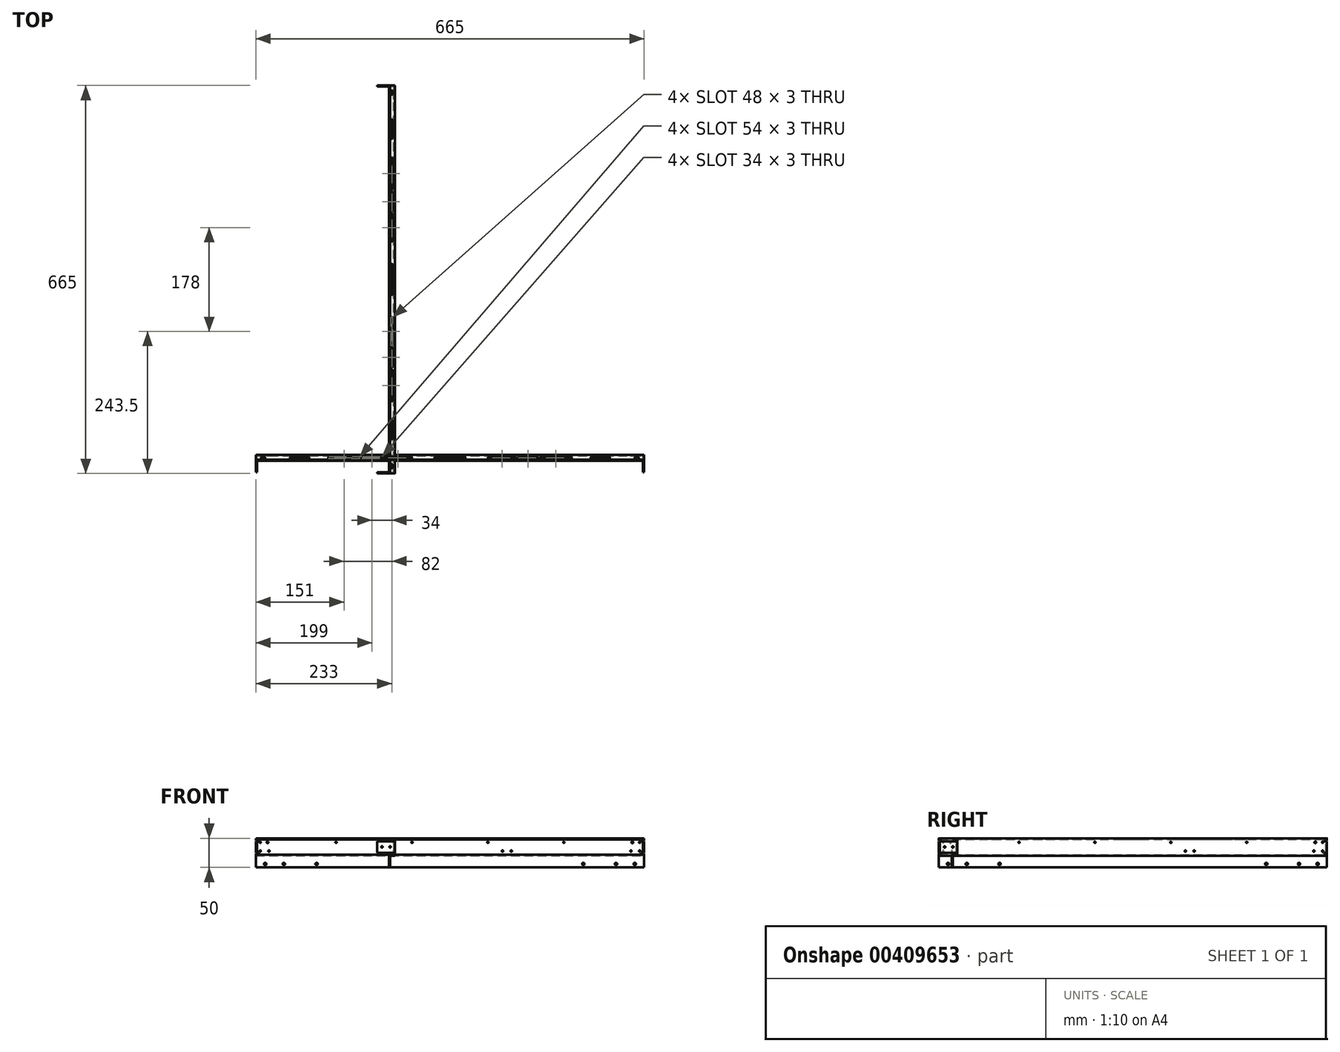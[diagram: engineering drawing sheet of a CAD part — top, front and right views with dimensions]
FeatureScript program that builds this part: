
annotation { "Feature Type Name" : "Feature", "Feature Type Description" : "" }
export const myFeature = defineFeature(function(context is Context, id is Id, definition is map)
    precondition{}
    {
        {
            var Q0;
            Q0=qCreatedBy(makeId("Front.planeOp"),FACE);
            var sketch = newSketch(context, id + "F0", { "sketchPlane" : qUnion([Q0])});
            skLineSegment(sketch, "E0", {"start": v(-20, 60) * mm, "end": v(-12, 60) * mm});
            skLineSegment(sketch, "E1", {"start": v(-12, 60) * mm, "end": v(-12, 58) * mm});
            skLineSegment(sketch, "E2", {"start": v(-12, 58) * mm, "end": v(-18, 58) * mm});
            skLineSegment(sketch, "E3", {"start": v(-18, 58) * mm, "end": v(-18, 32) * mm});
            skLineSegment(sketch, "E4", {"start": v(-20, 30) * mm, "end": v(-20, 60) * mm});
            skLineSegment(sketch, "E5.bottom", {"start": v(-18, 32) * mm, "end": v(-10, 32) * mm});
            skLineSegment(sketch, "E5.top", {"start": v(-20, 30) * mm, "end": v(-12, 30) * mm});
            skLineSegment(sketch, "E6.top", {"start": v(-10, 10) * mm, "end": v(-12, 10) * mm});
            skLineSegment(sketch, "E6.left", {"start": v(-10, 32) * mm, "end": v(-10, 10) * mm});
            skLineSegment(sketch, "E6.right", {"start": v(-12, 30) * mm, "end": v(-12, 10) * mm});
            skSolve(sketch);
        }
        {
            var Q0;
            Q0 = qSketchRegion(id + "F0", true);
            extrude(context, id + "F1", {"entities" : qUnion([Q0]), "depth" : 665 * mm});
        }
        {
            var Q0;
            Q0=makeQuery(id+"F1.opExtrude","SWEPT_FACE",FACE,{"disambiguationData":[OSD([sQuery(id+"F0.wireOp",EDGE,"E3")])]});
            var sketch = newSketch(context, id + "F2", { "sketchPlane" : qUnion([Q0])});
            skLineSegment(sketch, "E7.bottom", {"start": v(0, 35) * mm, "end": v(-2, 35) * mm});
            skLineSegment(sketch, "E7.top", {"start": v(0, 55) * mm, "end": v(-2, 55) * mm});
            skLineSegment(sketch, "E7.left", {"start": v(0, 35) * mm, "end": v(0, 55) * mm});
            skLineSegment(sketch, "E7.right", {"start": v(-2, 35) * mm, "end": v(-2, 55) * mm});
            skLineSegment(sketch, "E8.bottom", {"start": v(-665, 55) * mm, "end": v(-663, 55) * mm});
            skLineSegment(sketch, "E8.top", {"start": v(-665, 35) * mm, "end": v(-663, 35) * mm});
            skLineSegment(sketch, "E8.left", {"start": v(-665, 55) * mm, "end": v(-665, 35) * mm});
            skLineSegment(sketch, "E8.right", {"start": v(-663, 55) * mm, "end": v(-663, 35) * mm});
            skSolve(sketch);
        }
        {
            var Q0;
            Q0 = qSketchRegion(id + "F2", true);
            extrude(context, id + "F3", {"entities" : qUnion([Q0]), "operationType" : NewBodyOperationType.ADD, "depth" : 28 * mm});
        }
        {
            var Q0;
            Q0=makeQuery(id+"F1.opExtrude","SWEPT_FACE",FACE,{"disambiguationData":[OSD([sQuery(id+"F0.wireOp",EDGE,"E0")])]});
            var sketch = newSketch(context, id + "F4", { "sketchPlane" : qUnion([Q0])});
            skLineSegment(sketch, "E9.bottom", {"start": v(130, 0) * mm, "end": v(-20, 0) * mm, "construction": true});
            skLineSegment(sketch, "E9.top", {"start": v(130, -75) * mm, "end": v(-20, -75) * mm, "construction": true});
            skLineSegment(sketch, "E9.left", {"start": v(130, 0) * mm, "end": v(130, -75) * mm, "construction": true});
            skLineSegment(sketch, "E9.right", {"start": v(-20, 0) * mm, "end": v(-20, -75) * mm});
            skLineSegment(sketch, "E10.0", {"start": v(-20, -665) * mm, "end": v(-20, 0) * mm, "construction": true});
            skLineSegment(sketch, "E11.bottom", {"start": v(-20, -75) * mm, "end": v(130, -75) * mm, "construction": true});
            skLineSegment(sketch, "E11.top", {"start": v(-20, -140) * mm, "end": v(130, -140) * mm, "construction": true});
            skLineSegment(sketch, "E11.left", {"start": v(-20, -75) * mm, "end": v(-20, -140) * mm});
            skLineSegment(sketch, "E11.right", {"start": v(130, -75) * mm, "end": v(130, -140) * mm, "construction": true});
            skLineSegment(sketch, "E12.top", {"start": v(-20, -163) * mm, "end": v(130, -163) * mm, "construction": true});
            skLineSegment(sketch, "E12.left", {"start": v(-20, -140) * mm, "end": v(-20, -163) * mm});
            skLineSegment(sketch, "E12.right", {"start": v(130, -140) * mm, "end": v(130, -163) * mm, "construction": true});
            skLineSegment(sketch, "E13.top", {"start": v(-20, -243.5) * mm, "end": v(130, -243.5) * mm, "construction": true});
            skLineSegment(sketch, "E13.left", {"start": v(-20, -163) * mm, "end": v(-20, -243.5) * mm});
            skLineSegment(sketch, "E13.right", {"start": v(130, -163) * mm, "end": v(130, -243.5) * mm, "construction": true});
            skLineSegment(sketch, "E14.top", {"start": v(-20, -332.5) * mm, "end": v(130, -332.5) * mm, "construction": true});
            skLineSegment(sketch, "E14.left", {"start": v(-20, -243.5) * mm, "end": v(-20, -332.5) * mm});
            skLineSegment(sketch, "E14.right", {"start": v(130, -243.5) * mm, "end": v(130, -332.5) * mm, "construction": true});
            skLineSegment(sketch, "E15.top", {"start": v(-20, -462.5) * mm, "end": v(130, -462.5) * mm, "construction": true});
            skLineSegment(sketch, "E15.left", {"start": v(-20, -332.5) * mm, "end": v(-20, -462.5) * mm});
            skLineSegment(sketch, "E15.right", {"start": v(130, -332.5) * mm, "end": v(130, -462.5) * mm, "construction": true});
            skLineSegment(sketch, "E16.top", {"start": v(-20, -485.5) * mm, "end": v(130, -485.5) * mm, "construction": true});
            skLineSegment(sketch, "E16.left", {"start": v(-20, -462.5) * mm, "end": v(-20, -485.5) * mm});
            skLineSegment(sketch, "E16.right", {"start": v(130, -462.5) * mm, "end": v(130, -485.5) * mm, "construction": true});
            skLineSegment(sketch, "E17.top", {"start": v(-20, -665) * mm, "end": v(130, -665) * mm, "construction": true});
            skLineSegment(sketch, "E17.left", {"start": v(-20, -485.5) * mm, "end": v(-20, -665) * mm});
            skLineSegment(sketch, "E17.right", {"start": v(130, -485.5) * mm, "end": v(130, -665) * mm, "construction": true});
            skCircle(sketch, "E18", {"center": v(-15, -12.5) * mm, "radius": 1.5 * mm, "construction": true});
            skCircle(sketch, "E19", {"center": v(-15, -652.5) * mm, "radius": 1.5 * mm, "construction": true});
            skLineSegment(sketch, "E20.bottom", {"start": v(-13.5, -14.5) * mm, "end": v(-16.5, -14.5) * mm, "construction": true});
            skLineSegment(sketch, "E20.top", {"start": v(-13.5, -10.5) * mm, "end": v(-16.5, -10.5) * mm, "construction": true});
            skLineSegment(sketch, "E20.left", {"start": v(-13.5, -14.5) * mm, "end": v(-13.5, -10.5) * mm});
            skLineSegment(sketch, "E20.right", {"start": v(-16.5, -14.5) * mm, "end": v(-16.5, -10.5) * mm});
            skArc(sketch, "E21", {"start": v(-13.5, -10.5) * mm, "mid": v(-15, -9) * mm, "end": v(-16.5, -10.5) * mm});
            skArc(sketch, "E22", {"start": v(-16.5, -14.5) * mm, "mid": v(-15, -16) * mm, "end": v(-13.5, -14.5) * mm});
            skLineSegment(sketch, "E23.bottom", {"start": v(-13.5, -654.5) * mm, "end": v(-16.5, -654.5) * mm, "construction": true});
            skLineSegment(sketch, "E23.top", {"start": v(-13.5, -650.5) * mm, "end": v(-16.5, -650.5) * mm, "construction": true});
            skLineSegment(sketch, "E23.left", {"start": v(-13.5, -654.5) * mm, "end": v(-13.5, -650.5) * mm});
            skLineSegment(sketch, "E23.right", {"start": v(-16.5, -654.5) * mm, "end": v(-16.5, -650.5) * mm});
            skArc(sketch, "E24", {"start": v(-13.5, -650.5) * mm, "mid": v(-15, -649) * mm, "end": v(-16.5, -650.5) * mm});
            skArc(sketch, "E25", {"start": v(-16.5, -654.5) * mm, "mid": v(-15, -656) * mm, "end": v(-13.5, -654.5) * mm});
            skLineSegment(sketch, "E26", {"start": v(29.84, -27) * mm, "end": v(91.74, -27) * mm, "construction": true});
            skLineSegment(sketch, "E27", {"start": v(29.87, -48) * mm, "end": v(95.32, -48) * mm, "construction": true});
            skLineSegment(sketch, "E28.bottom", {"start": v(-13.5, -90) * mm, "end": v(-16.5, -90) * mm, "construction": true});
            skLineSegment(sketch, "E28.top", {"start": v(-13.5, -60) * mm, "end": v(-16.5, -60) * mm, "construction": true});
            skLineSegment(sketch, "E28.left", {"start": v(-13.5, -90) * mm, "end": v(-13.5, -60) * mm});
            skLineSegment(sketch, "E28.right", {"start": v(-16.5, -90) * mm, "end": v(-16.5, -60) * mm});
            skPoint(sketch, "E28.middle", {"position": v(-15, -75) * mm});
            skArc(sketch, "E29", {"start": v(-13.5, -60) * mm, "mid": v(-15, -58.5) * mm, "end": v(-16.5, -60) * mm});
            skArc(sketch, "E30", {"start": v(-16.5, -90) * mm, "mid": v(-15, -91.5) * mm, "end": v(-13.5, -90) * mm});
            skLineSegment(sketch, "E31.bottom", {"start": v(-13.5, -176.5) * mm, "end": v(-16.5, -176.5) * mm, "construction": true});
            skLineSegment(sketch, "E31.top", {"start": v(-13.5, -125.5) * mm, "end": v(-16.5, -125.5) * mm, "construction": true});
            skLineSegment(sketch, "E31.left", {"start": v(-13.5, -176.5) * mm, "end": v(-13.5, -125.5) * mm});
            skLineSegment(sketch, "E31.right", {"start": v(-16.5, -176.5) * mm, "end": v(-16.5, -125.5) * mm});
            skPoint(sketch, "E31.middle", {"position": v(-15, -151) * mm});
            skArc(sketch, "E32", {"start": v(-13.5, -125.5) * mm, "mid": v(-15, -124) * mm, "end": v(-16.5, -125.5) * mm});
            skArc(sketch, "E33", {"start": v(-16.5, -176.5) * mm, "mid": v(-15, -178) * mm, "end": v(-13.5, -176.5) * mm});
            skLineSegment(sketch, "E34", {"start": v(-372.96, -332.5) * mm, "end": v(602.04, -332.5) * mm, "construction": true});
            skLineSegment(sketch, "E35.bottom", {"start": v(-13.5, -266) * mm, "end": v(-16.5, -266) * mm, "construction": true});
            skLineSegment(sketch, "E35.top", {"start": v(-13.5, -221) * mm, "end": v(-16.5, -221) * mm, "construction": true});
            skLineSegment(sketch, "E35.left", {"start": v(-13.5, -266) * mm, "end": v(-13.5, -221) * mm});
            skLineSegment(sketch, "E35.right", {"start": v(-16.5, -266) * mm, "end": v(-16.5, -221) * mm});
            skPoint(sketch, "E35.middle", {"position": v(-15, -243.5) * mm});
            skArc(sketch, "E36", {"start": v(-13.5, -221) * mm, "mid": v(-15, -219.5) * mm, "end": v(-16.5, -221) * mm});
            skArc(sketch, "E37", {"start": v(-16.5, -266) * mm, "mid": v(-15, -267.5) * mm, "end": v(-13.5, -266) * mm});
            skLineSegment(sketch, "E38.bottom", {"start": v(-13.5, -357.5) * mm, "end": v(-16.5, -357.5) * mm, "construction": true});
            skLineSegment(sketch, "E38.top", {"start": v(-13.5, -307.5) * mm, "end": v(-16.5, -307.5) * mm, "construction": true});
            skLineSegment(sketch, "E38.left", {"start": v(-13.5, -357.5) * mm, "end": v(-13.5, -307.5) * mm});
            skLineSegment(sketch, "E38.right", {"start": v(-16.5, -357.5) * mm, "end": v(-16.5, -307.5) * mm});
            skPoint(sketch, "E38.middle", {"position": v(-15, -332.5) * mm});
            skArc(sketch, "E39", {"start": v(-13.5, -307.5) * mm, "mid": v(-15, -306) * mm, "end": v(-16.5, -307.5) * mm});
            skArc(sketch, "E40", {"start": v(-16.5, -357.5) * mm, "mid": v(-15, -359) * mm, "end": v(-13.5, -357.5) * mm});
            skLineSegment(sketch, "E41.bottom", {"start": v(-13.5, -214.5) * mm, "end": v(-16.5, -214.5) * mm, "construction": true});
            skLineSegment(sketch, "E41.top", {"start": v(-13.5, -183.5) * mm, "end": v(-16.5, -183.5) * mm, "construction": true});
            skLineSegment(sketch, "E41.left", {"start": v(-13.5, -214.5) * mm, "end": v(-13.5, -183.5) * mm});
            skLineSegment(sketch, "E41.right", {"start": v(-16.5, -214.5) * mm, "end": v(-16.5, -183.5) * mm});
            skPoint(sketch, "E41.middle", {"position": v(-15, -199) * mm});
            skArc(sketch, "E42", {"start": v(-13.5, -183.5) * mm, "mid": v(-15, -182) * mm, "end": v(-16.5, -183.5) * mm});
            skArc(sketch, "E43", {"start": v(-16.5, -214.5) * mm, "mid": v(-15, -216) * mm, "end": v(-13.5, -214.5) * mm});
            skArc(sketch, "E44.MirrorCS", {"start": v(-16.5, -450.5) * mm, "mid": v(-15, -449) * mm, "end": v(-13.5, -450.5) * mm});
            skLineSegment(sketch, "E45.MirrorCS", {"start": v(-13.5, -481.5) * mm, "end": v(-16.5, -481.5) * mm, "construction": true});
            skArc(sketch, "E46.MirrorCS", {"start": v(-13.5, -539.5) * mm, "mid": v(-15, -541) * mm, "end": v(-16.5, -539.5) * mm});
            skLineSegment(sketch, "E47.MirrorCS", {"start": v(-13.5, -444) * mm, "end": v(-16.5, -444) * mm, "construction": true});
            skArc(sketch, "E48.MirrorCS", {"start": v(-16.5, -399) * mm, "mid": v(-15, -397.5) * mm, "end": v(-13.5, -399) * mm});
            skArc(sketch, "E49.MirrorCS", {"start": v(-16.5, -488.5) * mm, "mid": v(-15, -487) * mm, "end": v(-13.5, -488.5) * mm});
            skArc(sketch, "E50.MirrorCS", {"start": v(-13.5, -444) * mm, "mid": v(-15, -445.5) * mm, "end": v(-16.5, -444) * mm});
            skArc(sketch, "E51.MirrorCS", {"start": v(-13.5, -481.5) * mm, "mid": v(-15, -483) * mm, "end": v(-16.5, -481.5) * mm});
            skLineSegment(sketch, "E52.MirrorCS", {"start": v(-13.5, -539.5) * mm, "end": v(-16.5, -539.5) * mm, "construction": true});
            skLineSegment(sketch, "E53.MirrorCS", {"start": v(-13.5, -488.5) * mm, "end": v(-16.5, -488.5) * mm, "construction": true});
            skLineSegment(sketch, "E54.MirrorCS", {"start": v(-13.5, -399) * mm, "end": v(-16.5, -399) * mm, "construction": true});
            skArc(sketch, "E55.MirrorCS", {"start": v(-16.5, -575) * mm, "mid": v(-15, -573.5) * mm, "end": v(-13.5, -575) * mm});
            skArc(sketch, "E56.MirrorCS", {"start": v(-13.5, -605) * mm, "mid": v(-15, -606.5) * mm, "end": v(-16.5, -605) * mm});
            skLineSegment(sketch, "E57.MirrorCS", {"start": v(-13.5, -605) * mm, "end": v(-16.5, -605) * mm, "construction": true});
            skLineSegment(sketch, "E58.MirrorCS", {"start": v(-13.5, -450.5) * mm, "end": v(-16.5, -450.5) * mm, "construction": true});
            skLineSegment(sketch, "E59.MirrorCS", {"start": v(-13.5, -575) * mm, "end": v(-16.5, -575) * mm, "construction": true});
            skLineSegment(sketch, "E60.MirrorCS", {"start": v(-16.5, -575) * mm, "end": v(-16.5, -605) * mm});
            skLineSegment(sketch, "E61.MirrorCS", {"start": v(-13.5, -575) * mm, "end": v(-13.5, -605) * mm});
            skLineSegment(sketch, "E62.MirrorCS", {"start": v(-13.5, -450.5) * mm, "end": v(-13.5, -481.5) * mm});
            skLineSegment(sketch, "E63.MirrorCS", {"start": v(-16.5, -450.5) * mm, "end": v(-16.5, -481.5) * mm});
            skPoint(sketch, "E64.MirrorP", {"position": v(-15, -466) * mm});
            skPoint(sketch, "E65.MirrorP", {"position": v(-15, -421.5) * mm});
            skPoint(sketch, "E66.MirrorP", {"position": v(-15, -590) * mm});
            skPoint(sketch, "E67.MirrorP", {"position": v(-15, -514) * mm});
            skLineSegment(sketch, "E68.MirrorCS", {"start": v(-16.5, -399) * mm, "end": v(-16.5, -444) * mm});
            skLineSegment(sketch, "E69.MirrorCS", {"start": v(-13.5, -399) * mm, "end": v(-13.5, -444) * mm});
            skLineSegment(sketch, "E70.MirrorCS", {"start": v(-16.5, -488.5) * mm, "end": v(-16.5, -539.5) * mm});
            skLineSegment(sketch, "E71.MirrorCS", {"start": v(-13.5, -488.5) * mm, "end": v(-13.5, -539.5) * mm});
            skPoint(sketch, "E72", {"position": v(-26.56, -12.5) * mm});
            skPoint(sketch, "E73", {"position": v(-24.04, -62.5) * mm});
            skPoint(sketch, "E74", {"position": v(-23.35, -87.5) * mm});
            skPoint(sketch, "E75", {"position": v(-24.4, -127.5) * mm});
            skPoint(sketch, "E76", {"position": v(-25, -145) * mm});
            skPoint(sketch, "E77", {"position": v(-24.92, -158) * mm});
            skPoint(sketch, "E78", {"position": v(-24.79, -174.5) * mm});
            skPoint(sketch, "E79", {"position": v(-24.35, -230) * mm});
            skPoint(sketch, "E80", {"position": v(-25.65, -255) * mm});
            skPoint(sketch, "E81", {"position": v(-24.26, -320) * mm});
            skPoint(sketch, "E82", {"position": v(-23.72, -352.5) * mm});
            skPoint(sketch, "E83", {"position": v(-24.95, -442.5) * mm});
            skPoint(sketch, "E84", {"position": v(-23.34, -467.5) * mm});
            skPoint(sketch, "E85", {"position": v(-22.9, -480.5) * mm});
            skPoint(sketch, "E86", {"position": v(-24.58, -489.5) * mm});
            skPoint(sketch, "E87", {"position": v(-25.98, -652.5) * mm});
            skSolve(sketch);
        }
        {
            var Q0;
            Q0 = qSketchRegion(id + "F4", true);
            extrude(context, id + "F5", {"entities" : qUnion([Q0]), "operationType" : NewBodyOperationType.REMOVE, "oppositeDirection" : true, "depth" : 2 * mm});
        }
        {
            var Q0;
            Q0=makeQuery(id+"F1.opExtrude","SWEPT_FACE",FACE,{"disambiguationData":[OSD([sQuery(id+"F0.wireOp",EDGE,"E6.left")])]});
            var sketch = newSketch(context, id + "F6", { "sketchPlane" : qUnion([Q0])});
            skCircle(sketch, "E88", {"center": v(-16, 16) * mm, "radius": 2.05 * mm});
            skCircle(sketch, "E89", {"center": v(-617, 16) * mm, "radius": 2.05 * mm});
            skCircle(sketch, "E90", {"center": v(-104, 16) * mm, "radius": 2.05 * mm});
            skCircle(sketch, "E91", {"center": v(-7.5, 53) * mm, "radius": 1.2 * mm});
            skCircle(sketch, "E92.1.0.0", {"center": v(-137.5, 53) * mm, "radius": 1.2 * mm});
            skCircle(sketch, "E92.2.0.0", {"center": v(-267.5, 53) * mm, "radius": 1.2 * mm});
            skLineSegment(sketch, "E92.direction1", {"start": v(-7.5, 53) * mm, "end": v(-137.5, 53) * mm, "construction": true});
            skCircle(sketch, "E93.0.3.0", {"center": v(-397.5, 53) * mm, "radius": 1.2 * mm});
            skCircle(sketch, "E93.0.4.0", {"center": v(-527.5, 53) * mm, "radius": 1.2 * mm});
            skCircle(sketch, "E93.0.5.0", {"center": v(-657.5, 53) * mm, "radius": 1.2 * mm});
            skCircle(sketch, "E94", {"center": v(-48, 16) * mm, "radius": 2.05 * mm});
            skCircle(sketch, "E95", {"center": v(-649, 16) * mm, "radius": 2.05 * mm});
            skCircle(sketch, "E96", {"center": v(-561, 16) * mm, "radius": 2.05 * mm});
            skLineSegment(sketch, "E97", {"start": v(-2, 23.79) * mm, "end": v(-2, 13.85) * mm, "construction": true});
            skLineSegment(sketch, "E98", {"start": v(-663, 24.44) * mm, "end": v(-663, 15.87) * mm, "construction": true});
            skLineSegment(sketch, "E99.0", {"start": v(-665, 58) * mm, "end": v(-665, 55) * mm});
            skLineSegment(sketch, "E100.0", {"start": v(-665, 55) * mm, "end": v(-663, 55) * mm});
            skPoint(sketch, "E101.oppositeSnap0", {"position": v(-664, 55) * mm});
            skLineSegment(sketch, "E101.bottom", {"start": v(-665, 56) * mm, "end": v(-660, 56) * mm});
            skLineSegment(sketch, "E101.top", {"start": v(-665, 55) * mm, "end": v(-660, 55) * mm});
            skLineSegment(sketch, "E101.left", {"start": v(-665, 56) * mm, "end": v(-665, 55) * mm});
            skLineSegment(sketch, "E101.right", {"start": v(-660, 56) * mm, "end": v(-660, 55) * mm});
            skLineSegment(sketch, "E102.0", {"start": v(-665, 35) * mm, "end": v(-663, 35) * mm});
            skLineSegment(sketch, "E102.1", {"start": v(-665, 35) * mm, "end": v(-665, 32) * mm});
            skLineSegment(sketch, "E103.bottom", {"start": v(-665, 35) * mm, "end": v(-660, 35) * mm});
            skLineSegment(sketch, "E103.top", {"start": v(-665, 34) * mm, "end": v(-660, 34) * mm});
            skLineSegment(sketch, "E103.left", {"start": v(-665, 35) * mm, "end": v(-665, 34) * mm});
            skLineSegment(sketch, "E103.right", {"start": v(-660, 35) * mm, "end": v(-660, 34) * mm});
            skLineSegment(sketch, "E104.0", {"start": v(0, 58) * mm, "end": v(0, 55) * mm});
            skLineSegment(sketch, "E104.1", {"start": v(0, 55) * mm, "end": v(-2, 55) * mm});
            skLineSegment(sketch, "E104.2", {"start": v(0, 35) * mm, "end": v(-2, 35) * mm});
            skLineSegment(sketch, "E104.3", {"start": v(0, 35) * mm, "end": v(0, 32) * mm});
            skLineSegment(sketch, "E105.bottom", {"start": v(0, 55) * mm, "end": v(-5, 55) * mm});
            skLineSegment(sketch, "E105.top", {"start": v(0, 56) * mm, "end": v(-5, 56) * mm});
            skLineSegment(sketch, "E105.left", {"start": v(0, 55) * mm, "end": v(0, 56) * mm});
            skLineSegment(sketch, "E105.right", {"start": v(-5, 55) * mm, "end": v(-5, 56) * mm});
            skLineSegment(sketch, "E106.bottom", {"start": v(0, 35) * mm, "end": v(-5, 35) * mm});
            skLineSegment(sketch, "E106.top", {"start": v(0, 34) * mm, "end": v(-5, 34) * mm});
            skLineSegment(sketch, "E106.left", {"start": v(0, 35) * mm, "end": v(0, 34) * mm});
            skLineSegment(sketch, "E106.right", {"start": v(-5, 35) * mm, "end": v(-5, 34) * mm});
            skCircle(sketch, "E107", {"center": v(-7.5, 38) * mm, "radius": 1.2 * mm});
            skCircle(sketch, "E108", {"center": v(-657.5, 38) * mm, "radius": 1.2 * mm});
            skCircle(sketch, "E109", {"center": v(-22.5, 38) * mm, "radius": 1.2 * mm});
            skCircle(sketch, "E110", {"center": v(-642.5, 38) * mm, "radius": 1.2 * mm});
            skCircle(sketch, "E111", {"center": v(-227.5, 38) * mm, "radius": 1.2 * mm});
            skCircle(sketch, "E112", {"center": v(-242.5, 38) * mm, "radius": 1.2 * mm});
            skCircle(sketch, "E113", {"center": v(-20, 53) * mm, "radius": 1.5 * mm});
            skCircle(sketch, "E114", {"center": v(-645, 53) * mm, "radius": 1.5 * mm});
            skSolve(sketch);
        }
        {
            var Q0;
            Q0 = qSketchRegion(id + "F6", true);
            extrude(context, id + "F7", {"entities" : qUnion([Q0]), "operationType" : NewBodyOperationType.REMOVE, "oppositeDirection" : true, "depth" : 25 * mm});
        }
        {
            var Q0;
            Q0=makeQuery(id+"F3.boolean.opBoolean","MERGE",FACE,{"derivedFrom":[makeQuery(id+"F1.opExtrude","CAP_FACE",FACE,{"disambiguationData":[OSD([sQuery(id+"F0.wireOp",EDGE,"E0"),sQuery(id+"F0.wireOp",EDGE,"E1"),sQuery(id+"F0.wireOp",EDGE,"E2"),sQuery(id+"F0.wireOp",EDGE,"E3"),sQuery(id+"F0.wireOp",EDGE,"E4"),sQuery(id+"F0.wireOp",EDGE,"E5.bottom"),sQuery(id+"F0.wireOp",EDGE,"E5.top"),sQuery(id+"F0.wireOp",EDGE,"E6.top"),sQuery(id+"F0.wireOp",EDGE,"E6.left"),sQuery(id+"F0.wireOp",EDGE,"E6.right")])],"isStart":false}),makeQuery(id+"F3.opExtrude","SWEPT_FACE",FACE,{"disambiguationData":[OSD([sQuery(id+"F2.wireOp",EDGE,"E8.left")])]})]});
            var sketch = newSketch(context, id + "F8", { "sketchPlane" : qUnion([Q0])});
            skCircle(sketch, "E115", {"center": v(-12, 45) * mm, "radius": 1.2 * mm});
            skPoint(sketch, "E116", {"position": v(10, 45) * mm});
            skCircle(sketch, "E117", {"center": v(2, 45) * mm, "radius": 1.2 * mm});
            skSolve(sketch);
        }
        {
            var Q0;
            Q0 = qSketchRegion(id + "F8", true);
            extrude(context, id + "F9", {"entities" : qUnion([Q0]), "operationType" : NewBodyOperationType.REMOVE, "endBound" : BoundingType.THROUGH_ALL, "oppositeDirection" : true, "depth" : 2 * mm});
        }
        {
            var Q0;
            Q0=makeQuery(id+"F1.opExtrude","SWEPT_EDGE",EDGE,{"disambiguationData":[OSD([sQuery(id+"F0.wireOp",EDGE,"E0"),sQuery(id+"F0.wireOp",EDGE,"E4")])]});
            var Q1;
            Q1=makeQuery(id+"F1.opExtrude","SWEPT_EDGE",EDGE,{"disambiguationData":[OSD([sQuery(id+"F0.wireOp",EDGE,"E2"),sQuery(id+"F0.wireOp",EDGE,"E3")])]});
            var Q2;
            Q2=makeQuery(id+"F1.opExtrude","SWEPT_EDGE",EDGE,{"disambiguationData":[OSD([sQuery(id+"F0.wireOp",EDGE,"E3"),sQuery(id+"F0.wireOp",EDGE,"E5.bottom")])]});
            var Q3;
            Q3=makeQuery(id+"F1.opExtrude","SWEPT_EDGE",EDGE,{"disambiguationData":[OSD([sQuery(id+"F0.wireOp",EDGE,"E5.bottom"),sQuery(id+"F0.wireOp",EDGE,"E6.left")])]});
            var Q4;
            Q4=makeQuery(id+"F1.opExtrude","SWEPT_EDGE",EDGE,{"disambiguationData":[OSD([sQuery(id+"F0.wireOp",EDGE,"E4"),sQuery(id+"F0.wireOp",EDGE,"E5.top")])]});
            var Q5;
            Q5=makeQuery(id+"F1.opExtrude","SWEPT_EDGE",EDGE,{"disambiguationData":[OSD([sQuery(id+"F0.wireOp",EDGE,"E5.top"),sQuery(id+"F0.wireOp",EDGE,"E6.right")])]});
            fillet(context, id + "F10", {"entities" : qUnion([Q0, Q1, Q2, Q3, Q4, Q5]), "radius" : 1 * mm, "tangentPropagation" : true, "allowEdgeOverflow" : false});
        }
        {
            var Q0;
            Q0=makeQuery(id+"F3.opExtrude","CAP_EDGE",EDGE,{"disambiguationData":[OSD([sQuery(id+"F2.wireOp",EDGE,"E8.right")])],"isStart":true});
            var Q1;
            {var subQ0=sQuery(id+"F0.wireOp",EDGE,"E4");Q1=makeQuery(id+"F7.boolean.opBoolean","SPLIT",EDGE,{"disambiguationData":[TD([makeQuery(id+"F3.opExtrude","SWEPT_FACE",FACE,{"disambiguationData":[OSD([sQuery(id+"F2.wireOp",EDGE,"E8.bottom")])]})])],"derivedFrom":makeQuery(id+"F1.opExtrude","CAP_EDGE",EDGE,{"disambiguationData":[OSD([subQ0])],"isStart":false})});}
            var Q2;
            Q2=makeQuery(id+"F3.opExtrude","CAP_EDGE",EDGE,{"disambiguationData":[OSD([sQuery(id+"F2.wireOp",EDGE,"E7.right")])],"isStart":true});
            var Q3;
            {var subQ0=sQuery(id+"F0.wireOp",EDGE,"E4");Q3=makeQuery(id+"F7.boolean.opBoolean","SPLIT",EDGE,{"disambiguationData":[TD([makeQuery(id+"F3.opExtrude","SWEPT_FACE",FACE,{"disambiguationData":[OSD([sQuery(id+"F2.wireOp",EDGE,"E7.bottom")])]})])],"derivedFrom":makeQuery(id+"F1.opExtrude","CAP_EDGE",EDGE,{"disambiguationData":[OSD([subQ0])],"isStart":true})});}
            fillet(context, id + "F11", {"entities" : qUnion([Q0, Q1, Q2, Q3]), "radius" : 1 * mm, "tangentPropagation" : true, "allowEdgeOverflow" : false});
        }
        {
            var Q0;
            Q0=qCreatedBy(makeId("Right.planeOp"),FACE);
            cPlane(context, id + "F12", {"entities" : qUnion([Q0]), "cplaneType" : CPlaneType.OFFSET, "offset" : 113 * mm, "width" : 150 * mm, "height" : 150 * mm});
        }
        {
            var Q0;
            Q0=makeQuery(id+"F1.opExtrude","SWEPT_BODY",BODY,{"disambiguationData":[OSD([sQuery(id+"F0.wireOp",EDGE,"E0"),sQuery(id+"F0.wireOp",EDGE,"E1"),sQuery(id+"F0.wireOp",EDGE,"E2"),sQuery(id+"F0.wireOp",EDGE,"E3"),sQuery(id+"F0.wireOp",EDGE,"xb1tLthF-IiVW-rdyS-DzM4-F0JxlruL6ZiX"),sQuery(id+"F0.wireOp",EDGE,"E4")])]});
            var Q1;
            Q1=qCreatedBy(id+"F12.planeOp",FACE);
            mirror(context, id + "F13", {"entities" : qUnion([Q0]), "mirrorPlane" : qUnion([Q1])});
        }
        {
            var Q0;
            Q0=makeQuery(id+"F1.opExtrude","SWEPT_BODY",BODY,{"disambiguationData":[OSD([sQuery(id+"F0.wireOp",EDGE,"E0"),sQuery(id+"F0.wireOp",EDGE,"E1"),sQuery(id+"F0.wireOp",EDGE,"E2"),sQuery(id+"F0.wireOp",EDGE,"E3"),sQuery(id+"F0.wireOp",EDGE,"E4"),sQuery(id+"F0.wireOp",EDGE,"E5.bottom"),sQuery(id+"F0.wireOp",EDGE,"E5.top"),sQuery(id+"F0.wireOp",EDGE,"E6.top"),sQuery(id+"F0.wireOp",EDGE,"E6.left"),sQuery(id+"F0.wireOp",EDGE,"E6.right")])]});
            var Q1;
            Q1=makeQuery(id+"F3.opExtrude","CAP_EDGE",EDGE,{"disambiguationData":[OSD([sQuery(id+"F2.wireOp",EDGE,"E8.right")])],"isStart":false});
            transform(context, id + "F14", {"entities" : qUnion([Q0]), "transformType" : TransformType.ROTATION, "transformAxis" : qUnion([Q1]), "angle" : 90 * degree, "makeCopy" : false});
        }
    });
